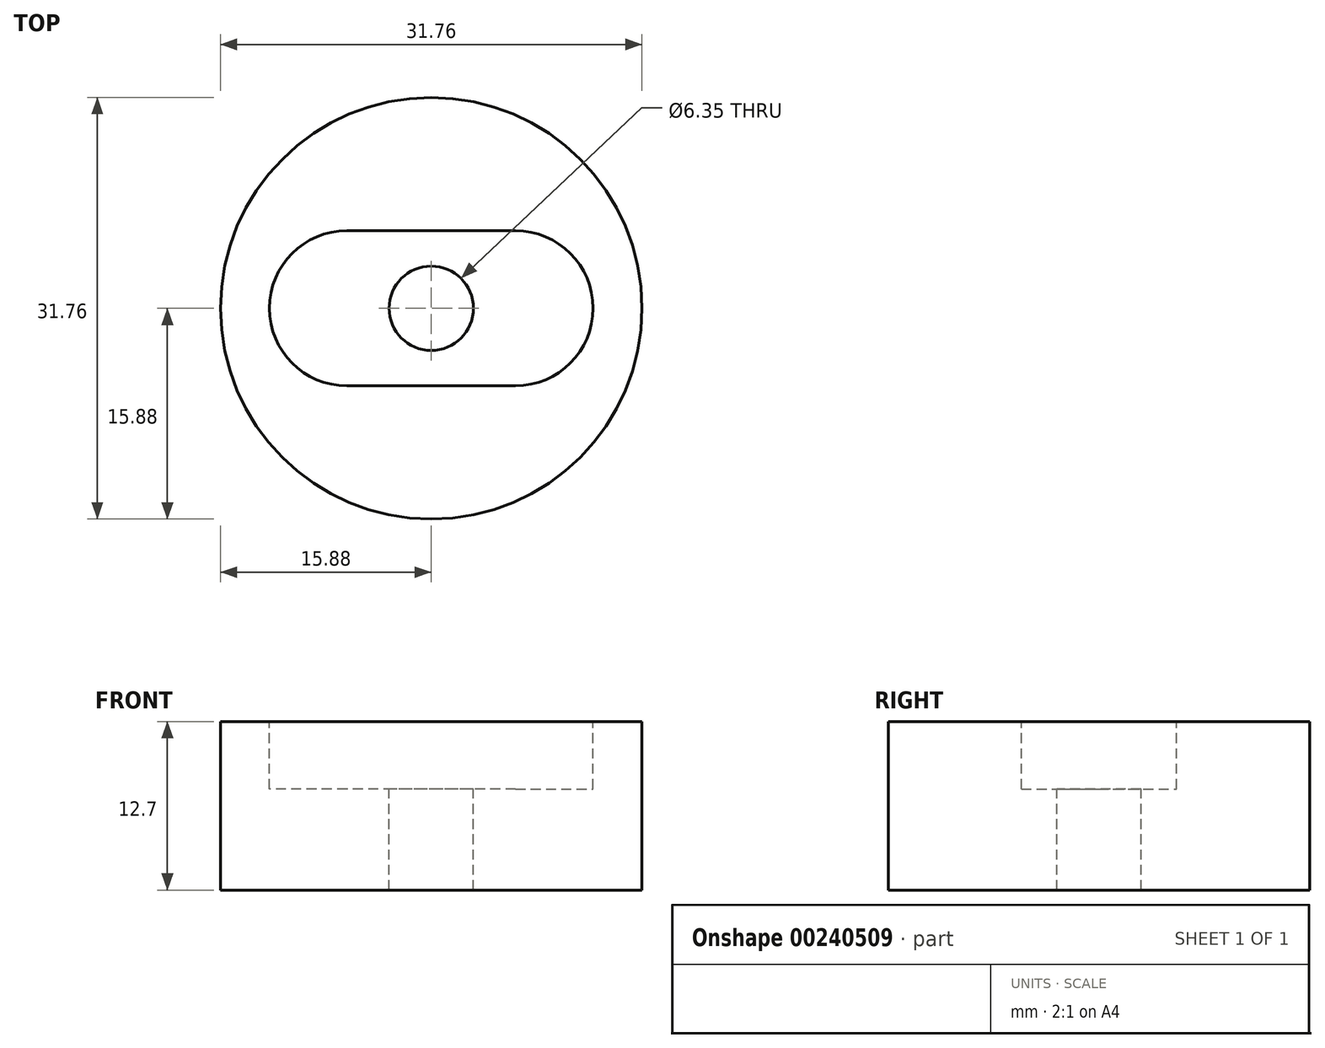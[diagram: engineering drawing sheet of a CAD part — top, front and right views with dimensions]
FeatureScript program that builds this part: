
annotation { "Feature Type Name" : "Feature", "Feature Type Description" : "" }
export const myFeature = defineFeature(function(context is Context, id is Id, definition is map)
    precondition{}
    {
        {
            var Q0;
            Q0=qCreatedBy(makeId("Top.planeOp"),FACE);
            var sketch = newSketch(context, id + "F0", { "sketchPlane" : qUnion([Q0])});
            skCircle(sketch, "E0", {"center": v(0, 0) * mm, "radius": 15.88 * mm});
            skSolve(sketch);
        }
        {
            var Q0;
            Q0 = qSketchRegion(id + "F0", true);
            extrude(context, id + "F1", {"entities" : qUnion([Q0]), "depth" : 12.7 * mm});
        }
        {
            var Q0;
            Q0=makeQuery(id+"F1.opExtrude","CAP_FACE",FACE,{"disambiguationData":[OSD([sQuery(id+"F0.wireOp",EDGE,"E0")])],"isStart":false});
            var sketch = newSketch(context, id + "F2", { "sketchPlane" : qUnion([Q0])});
            skCircle(sketch, "E1", {"center": v(0, 0) * mm, "radius": 3.18 * mm});
            skSolve(sketch);
        }
        {
            var Q0;
            Q0 = qSketchRegion(id + "F2", true);
            var Q1;
            Q1=makeQuery(id+"F1.opExtrude","CAP_FACE",FACE,{"disambiguationData":[OSD([sQuery(id+"F0.wireOp",EDGE,"E0")])],"isStart":true});
            extrude(context, id + "F3", {"entities" : qUnion([Q0]), "operationType" : NewBodyOperationType.REMOVE, "endBound" : BoundingType.UP_TO_SURFACE, "oppositeDirection" : true, "endBoundEntityFace" : qUnion([Q1]), "depth" : 25.4 * mm});
        }
        {
            var Q0;
            Q0=makeQuery(id+"F1.opExtrude","CAP_FACE",FACE,{"disambiguationData":[OSD([sQuery(id+"F0.wireOp",EDGE,"E0")])],"isStart":false});
            var sketch = newSketch(context, id + "F4", { "sketchPlane" : qUnion([Q0])});
            skLineSegment(sketch, "E2", {"start": v(-6.35, 5.84) * mm, "end": v(6.35, 5.84) * mm});
            skLineSegment(sketch, "E3", {"start": v(6.35, 5.84) * mm, "end": v(6.35, -5.84) * mm, "construction": true});
            skLineSegment(sketch, "E4", {"start": v(6.35, -5.84) * mm, "end": v(-6.35, -5.84) * mm});
            skLineSegment(sketch, "E5", {"start": v(-6.35, -5.84) * mm, "end": v(-6.35, 5.84) * mm, "construction": true});
            skPoint(sketch, "E6", {"position": v(0, 5.84) * mm});
            skPoint(sketch, "E7", {"position": v(-6.35, 0) * mm});
            skArc(sketch, "E8", {"start": v(6.35, -5.84) * mm, "mid": v(12.2, 0) * mm, "end": v(6.35, 5.84) * mm});
            skArc(sketch, "E9", {"start": v(-6.35, 5.84) * mm, "mid": v(-12.2, 0) * mm, "end": v(-6.35, -5.84) * mm});
            skSolve(sketch);
        }
        {
            var Q0;
            Q0 = qSketchRegion(id + "F4", true);
            extrude(context, id + "F5", {"entities" : qUnion([Q0]), "operationType" : NewBodyOperationType.REMOVE, "oppositeDirection" : true, "depth" : 5.08 * mm});
        }
    });
